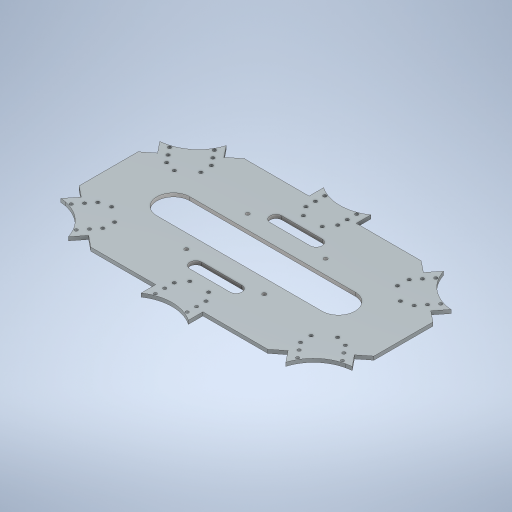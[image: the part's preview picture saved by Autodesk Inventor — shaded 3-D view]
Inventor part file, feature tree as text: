
AUTODESK INVENTOR PART (.ipt)
format: ipt  version: 2024 (Build 280153000, 153)  size: 484,864 bytes
history: native  units: in
note: dims shown in document units (in); Inventor stores cm internally (conversion verified against a paired STEP export)
features: extrude x1, sketch x1
ambient origin geometry x8: Origin, YZ Plane, XZ Plane, XY Plane, X Axis, Y Axis, Z Axis, Center Point
bodies: Solid1 (feature_tree)
feature tree (2):
  extrude  "Extrusion1"  Depth=0.1181in
  sketch  "Sketch1"  dims[d0=9.8425in d1=5.1181in d2=1.2598in d4=0.1043in d5=0.1043in d6=0.1043in d7=0.1043in d8=0.6299in d9=0.2165in d10=0.2165in d11=0.0984in d12=0.0984in d13=0.1043in d14=0.1043in d15=0.1043in d16=0.1043in d18=0.315in d19=0.315in d20=0.315in d21=0.315in d22=0.9843in d23=1.9685in d26=0.1181in d27=0.0in d28=0.5315in d29=0.1575in d41=0.1181in d42=1.0236in d43=1.2992in d44=1.1024in d45=2.1654in d46=2.1654in d47=1.3386in d48=4.252in d49=4.252in d50=0.1969in d51=0.1043in d52=0.1043in d53=0.1043in d54=0.1043in d55=0.1043in d56=0.1043in d57=0.1043in d58=0.1043in]
